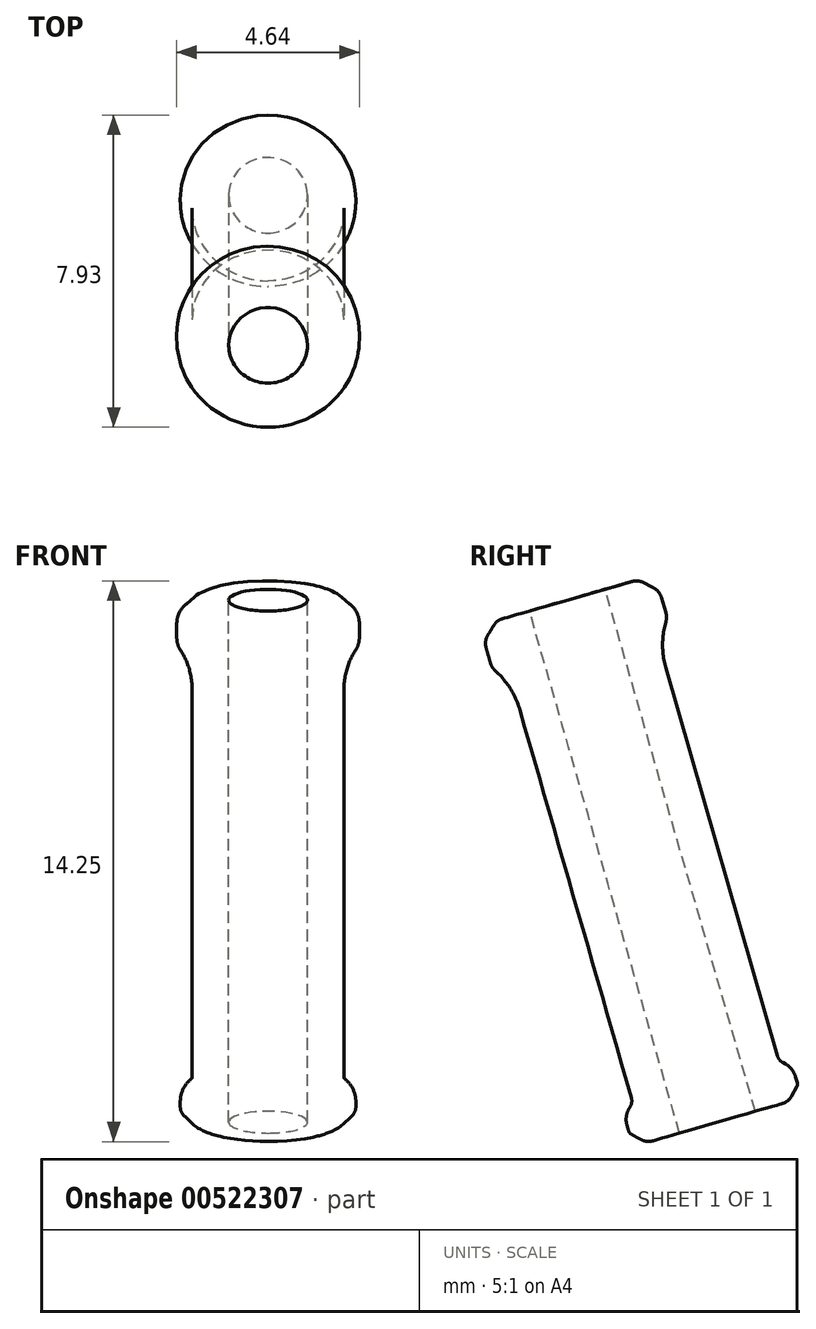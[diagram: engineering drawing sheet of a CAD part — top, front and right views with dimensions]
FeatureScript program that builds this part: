
annotation { "Feature Type Name" : "Feature", "Feature Type Description" : "" }
export const myFeature = defineFeature(function(context is Context, id is Id, definition is map)
    precondition{}
    {
        {
            var Q0;
            Q0=qCreatedBy(makeId("Right.planeOp"),FACE);
            var sketch = newSketch(context, id + "F0", { "sketchPlane" : qUnion([Q0])});
            skLineSegment(sketch, "E0", {"start": v(27.3, 28.44) * mm, "end": v(31.1, 15.18) * mm});
            skLineSegment(sketch, "E1", {"start": v(31.1, 15.18) * mm, "end": v(30.42, 14.98) * mm});
            skLineSegment(sketch, "E2", {"start": v(30.12, 15.01) * mm, "end": v(29.87, 15.15) * mm});
            skLineSegment(sketch, "E3", {"start": v(29.81, 15.23) * mm, "end": v(29.77, 15.38) * mm});
            skLineSegment(sketch, "E4", {"start": v(29.82, 15.8) * mm, "end": v(29.85, 15.86) * mm});
            skLineSegment(sketch, "E5", {"start": v(29.88, 16.08) * mm, "end": v(27.05, 25.93) * mm});
            skLineSegment(sketch, "E6", {"start": v(26.43, 26.92) * mm, "end": v(26.42, 26.93) * mm});
            skLineSegment(sketch, "E7", {"start": v(26.3, 27.12) * mm, "end": v(26.2, 27.5) * mm});
            skLineSegment(sketch, "E8", {"start": v(26.23, 27.83) * mm, "end": v(26.4, 28.09) * mm});
            skLineSegment(sketch, "E9", {"start": v(26.6, 28.24) * mm, "end": v(27.3, 28.44) * mm});
            skPoint(sketch, "E10.visualSharp", {"position": v(26.14, 27.68) * mm});
            skArc(sketch, "E10.filletArc", {"start": v(26.23, 27.83) * mm, "mid": v(26.18, 27.67) * mm, "end": v(26.2, 27.5) * mm});
            skPoint(sketch, "E11.visualSharp", {"position": v(26.33, 27) * mm});
            skArc(sketch, "E11.filletArc", {"start": v(26.3, 27.12) * mm, "mid": v(26.35, 27.02) * mm, "end": v(26.42, 26.93) * mm});
            skPoint(sketch, "E12.visualSharp", {"position": v(26.46, 28.2) * mm});
            skArc(sketch, "E12.filletArc", {"start": v(26.6, 28.24) * mm, "mid": v(26.48, 28.18) * mm, "end": v(26.4, 28.09) * mm});
            skPoint(sketch, "E13.visualSharp", {"position": v(26.88, 26.51) * mm});
            skArc(sketch, "E13.filletArc", {"start": v(27.05, 25.93) * mm, "mid": v(26.8, 26.47) * mm, "end": v(26.43, 26.92) * mm});
            skPoint(sketch, "E14.visualSharp", {"position": v(29.91, 15.96) * mm});
            skArc(sketch, "E14.filletArc", {"start": v(29.85, 15.86) * mm, "mid": v(29.89, 15.96) * mm, "end": v(29.88, 16.08) * mm});
            skPoint(sketch, "E15.visualSharp", {"position": v(29.7, 15.6) * mm});
            skArc(sketch, "E15.filletArc", {"start": v(29.82, 15.8) * mm, "mid": v(29.75, 15.59) * mm, "end": v(29.77, 15.38) * mm});
            skPoint(sketch, "E16.visualSharp", {"position": v(29.83, 15.18) * mm});
            skArc(sketch, "E16.filletArc", {"start": v(29.81, 15.23) * mm, "mid": v(29.83, 15.18) * mm, "end": v(29.87, 15.15) * mm});
            skPoint(sketch, "E17.visualSharp", {"position": v(30.26, 14.93) * mm});
            skArc(sketch, "E17.filletArc", {"start": v(30.12, 15.01) * mm, "mid": v(30.27, 14.97) * mm, "end": v(30.42, 14.98) * mm});
            skLineSegment(sketch, "E18.0", {"start": v(28.25, 28.72) * mm, "end": v(32.07, 15.45) * mm, "construction": true});
            skSolve(sketch);
        }
        {
            var Q0;
            Q0 = qSketchRegion(id + "F0", true);
            var Q1;
            Q1=sQuery(id+"F0.wireOp",EDGE,"E18.0");
            revolve(context, id + "F1", {"surfaceOperationType" : NewSurfaceOperationType.NEW, "entities" : qUnion([Q0]), "axis" : qUnion([Q1]), "revolveType" : RevolveType.FULL});
        }
    });
